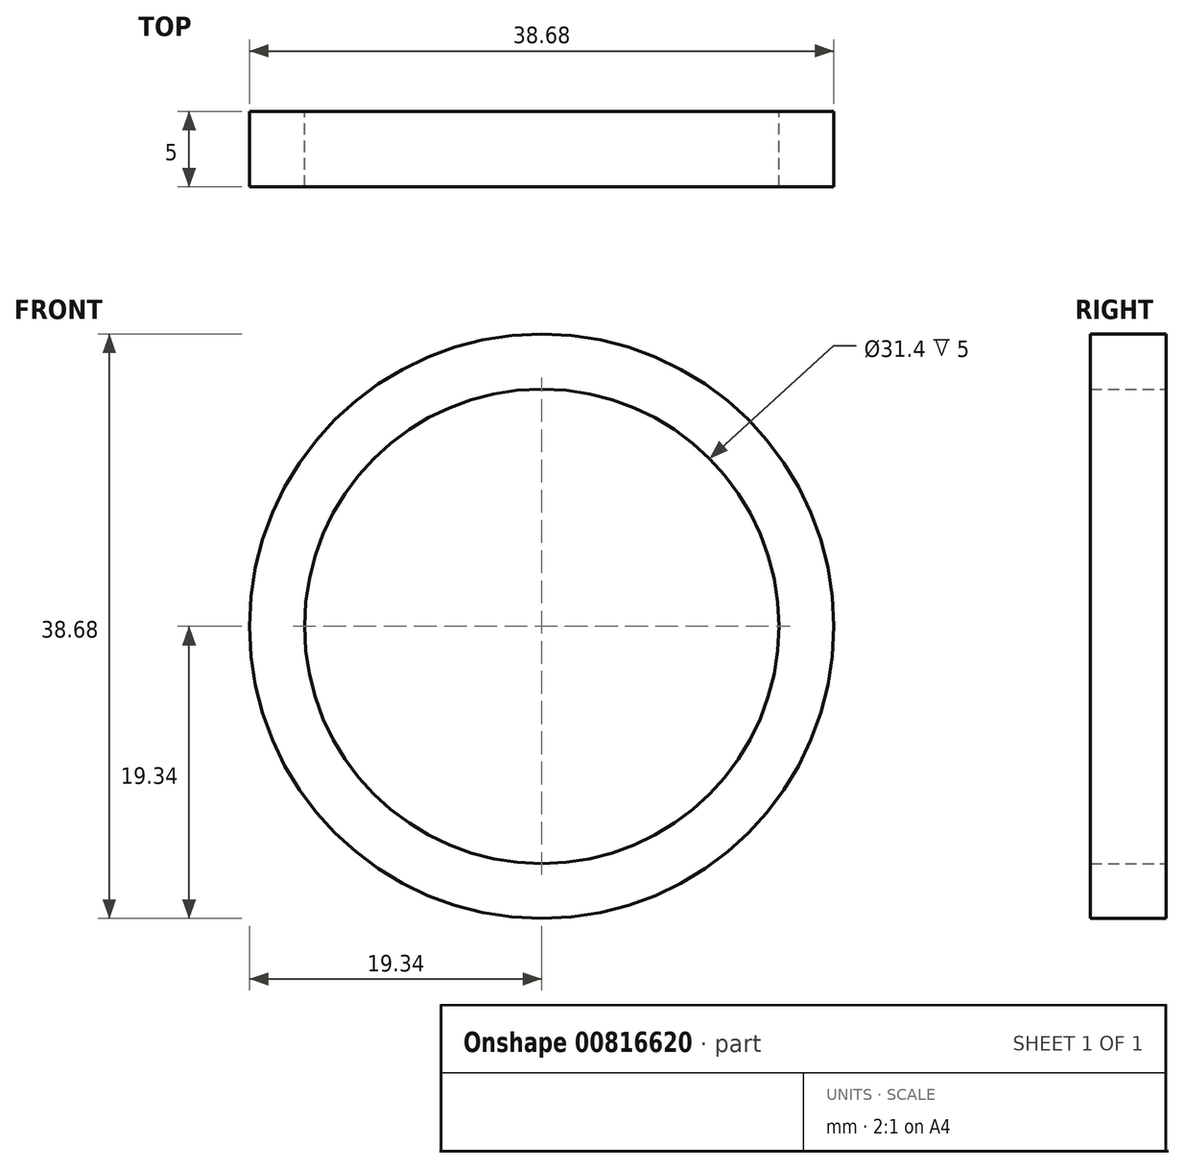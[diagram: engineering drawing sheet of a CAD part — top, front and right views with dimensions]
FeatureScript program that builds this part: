
annotation { "Feature Type Name" : "Feature", "Feature Type Description" : "" }
export const myFeature = defineFeature(function(context is Context, id is Id, definition is map)
    precondition{}
    {
        {
            var Q0;
            Q0=qCreatedBy(makeId("Front.planeOp"),FACE);
            var sketch = newSketch(context, id + "F0", { "sketchPlane" : qUnion([Q0])});
            skCircle(sketch, "E0", {"center": v(0, 0) * mm, "radius": 19.34 * mm});
            skCircle(sketch, "E1", {"center": v(0, 0) * mm, "radius": 15.7 * mm});
            skSolve(sketch);
        }
        {
            var Q0;
            Q0=makeQuery(id+"F0.imprint","IMPRINT",FACE,{"disambiguationData":[TD([[makeQuery(id+"F0.imprint","IMPRINT",EDGE,{"derivedFrom":sQuery(id+"F0.wireOp",EDGE,"E0")}),1.0]])]});
            extrude(context, id + "F1", {"entities" : qUnion([Q0]), "endBound" : BoundingType.SYMMETRIC, "depth" : 5 * mm, "offsetDistance" : 25 * mm});
        }
    });
